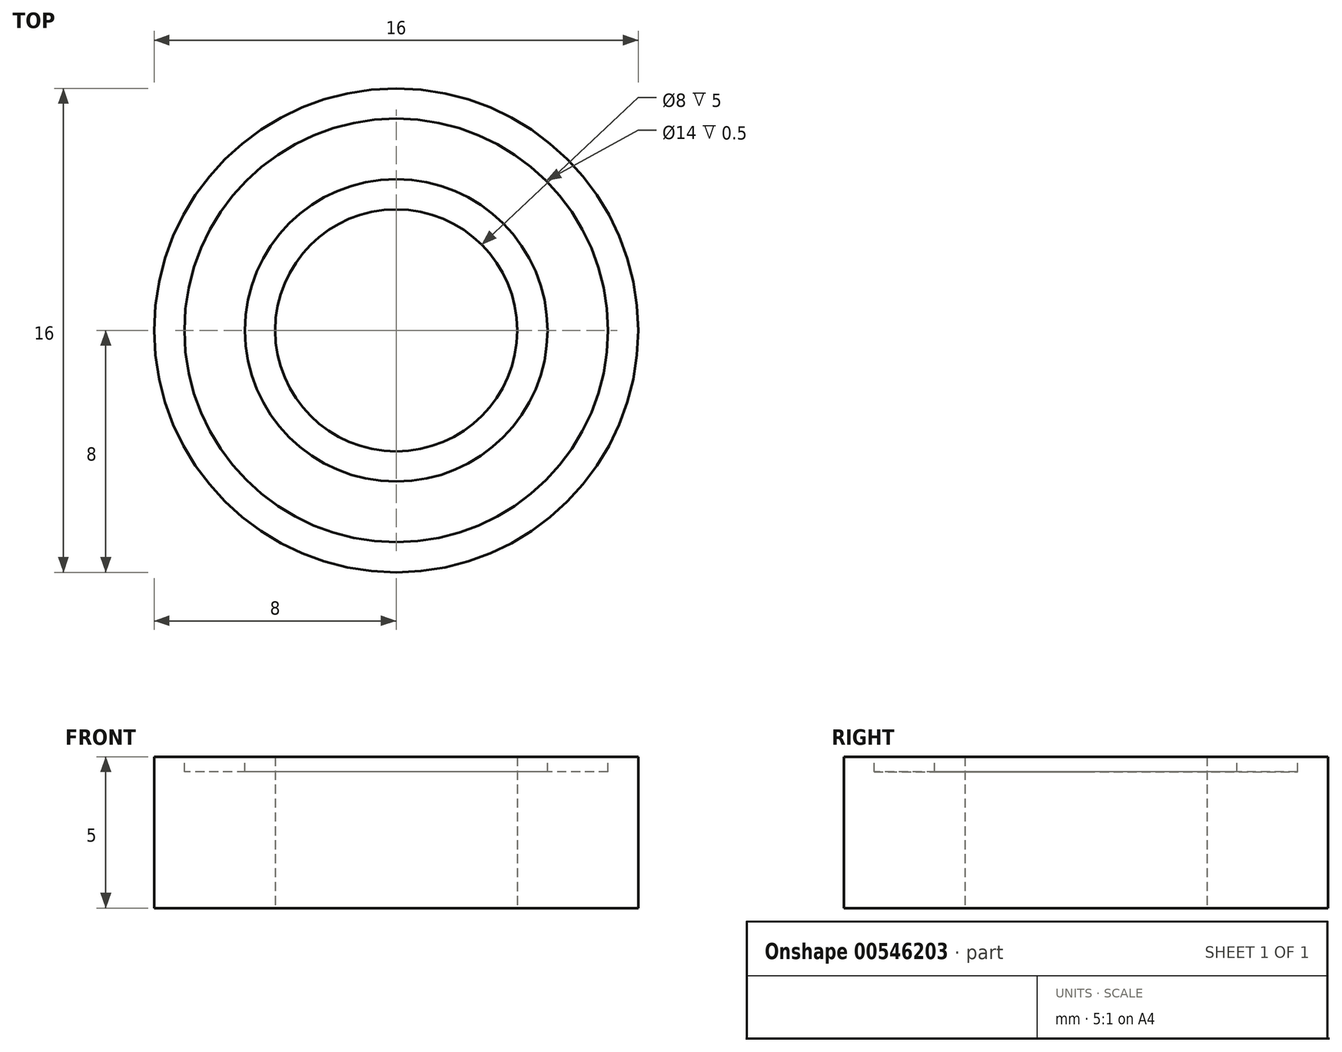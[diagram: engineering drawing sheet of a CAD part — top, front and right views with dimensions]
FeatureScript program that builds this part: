
annotation { "Feature Type Name" : "Feature", "Feature Type Description" : "" }
export const myFeature = defineFeature(function(context is Context, id is Id, definition is map)
    precondition{}
    {
        {
            var Q0;
            Q0=qCreatedBy(makeId("Top.planeOp"),FACE);
            var sketch = newSketch(context, id + "F0", { "sketchPlane" : qUnion([Q0])});
            skCircle(sketch, "E0", {"center": v(0, 0) * mm, "radius": 8 * mm});
            skCircle(sketch, "E1", {"center": v(0, 0) * mm, "radius": 4 * mm});
            skSolve(sketch);
        }
        {
            var Q0;
            Q0=qSketchRegion(id+"F0",true);
            extrude(context, id + "F1", {"entities" : qUnion([Q0]), "depth" : 5 * mm});
        }
        {
            var Q0;
            Q0=makeQuery(id+"F1.opExtrude","CAP_FACE",FACE,{"disambiguationData":[OSD([sQuery(id+"F0.wireOp",EDGE,"E0"),sQuery(id+"F0.wireOp",EDGE,"E1")])],"isStart":false});
            var sketch = newSketch(context, id + "F2", { "sketchPlane" : qUnion([Q0])});
            skCircle(sketch, "E2", {"center": v(0, 0) * mm, "radius": 5 * mm});
            skCircle(sketch, "E3", {"center": v(0, 0) * mm, "radius": 7 * mm});
            skSolve(sketch);
        }
        {
            var Q0;
            Q0=makeQuery(id+"F2.imprint","IMPRINT",FACE,{"disambiguationData":[TD([[makeQuery(id+"F2.imprint","IMPRINT",EDGE,{"derivedFrom":sQuery(id+"F2.wireOp",EDGE,"E2")}),-1.0]])]});
            extrude(context, id + "F3", {"entities" : qUnion([Q0]), "operationType" : NewBodyOperationType.REMOVE, "oppositeDirection" : true, "depth" : .5 * mm});
        }
    });
